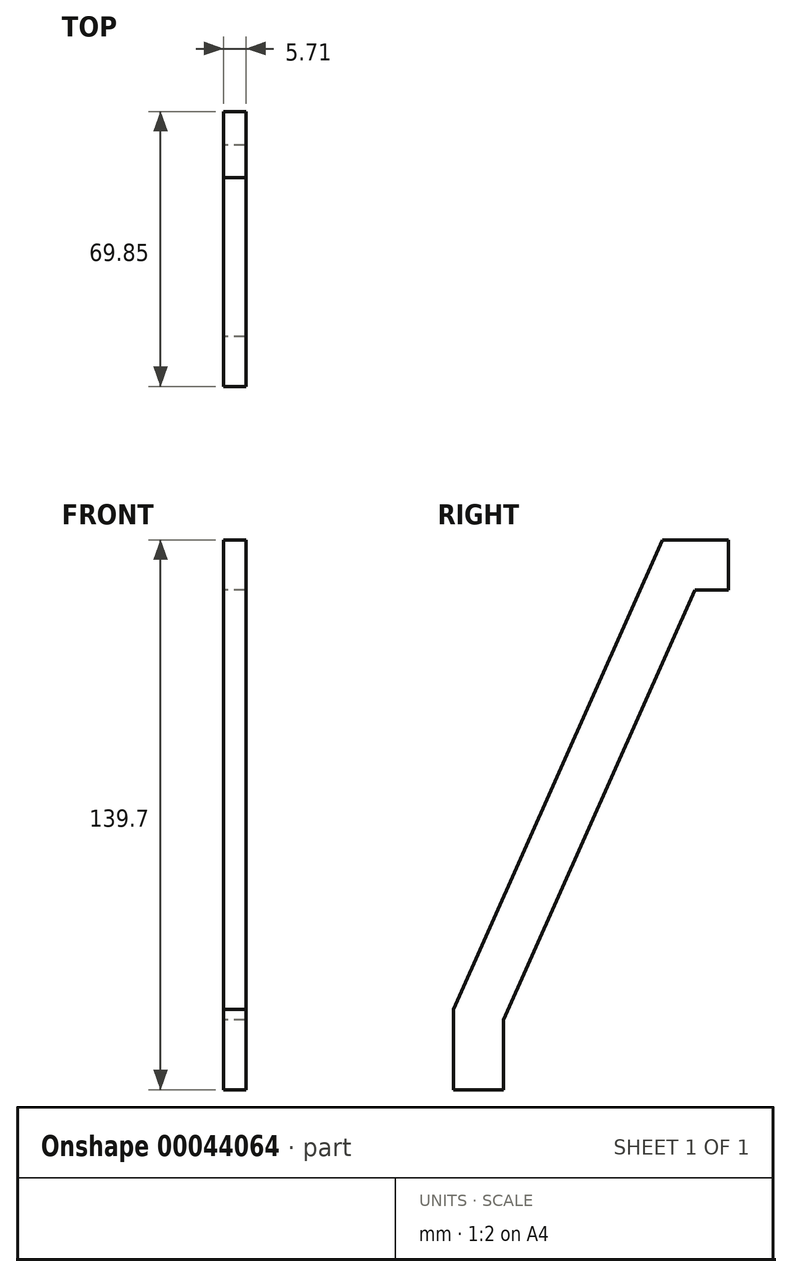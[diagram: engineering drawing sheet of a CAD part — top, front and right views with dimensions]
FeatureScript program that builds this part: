
annotation { "Feature Type Name" : "Feature", "Feature Type Description" : "" }
export const myFeature = defineFeature(function(context is Context, id is Id, definition is map)
    precondition{}
    {
        {
            var Q0;
            Q0=qCreatedBy(makeId("Right.planeOp"),FACE);
            var sketch = newSketch(context, id + "F0", { "sketchPlane" : qUnion([Q0])});
            skLineSegment(sketch, "E0", {"start": v(0, 0) * mm, "end": v(0, 12.7) * mm, "construction": true});
            skLineSegment(sketch, "E1", {"start": v(0, 12.7) * mm, "end": v(50.8, 127) * mm, "construction": true});
            skLineSegment(sketch, "E2", {"start": v(50.8, 127) * mm, "end": v(63.5, 127) * mm, "construction": true});
            skLineSegment(sketch, "E3.0", {"start": v(54.93, 120.65) * mm, "end": v(63.5, 120.65) * mm});
            skLineSegment(sketch, "E3.1", {"start": v(6.35, 11.35) * mm, "end": v(54.93, 120.65) * mm});
            skLineSegment(sketch, "E3.2", {"start": v(6.35, -6.35) * mm, "end": v(6.35, 11.35) * mm});
            skLineSegment(sketch, "E4.0", {"start": v(46.67, 133.35) * mm, "end": v(63.5, 133.35) * mm});
            skLineSegment(sketch, "E4.1", {"start": v(-6.35, 14.05) * mm, "end": v(46.67, 133.35) * mm});
            skLineSegment(sketch, "E4.2", {"start": v(-6.35, -6.35) * mm, "end": v(-6.35, 14.05) * mm});
            skLineSegment(sketch, "E5", {"start": v(-6.35, -6.35) * mm, "end": v(6.35, -6.35) * mm});
            skLineSegment(sketch, "E6", {"start": v(63.5, 120.65) * mm, "end": v(63.5, 133.35) * mm});
            skSolve(sketch);
        }
        {
            var Q0;
            Q0 = qSketchRegion(id + "F0", true);
            extrude(context, id + "F1", {"entities" : qUnion([Q0]), "depth" : 5.7 * mm});
        }
    });
